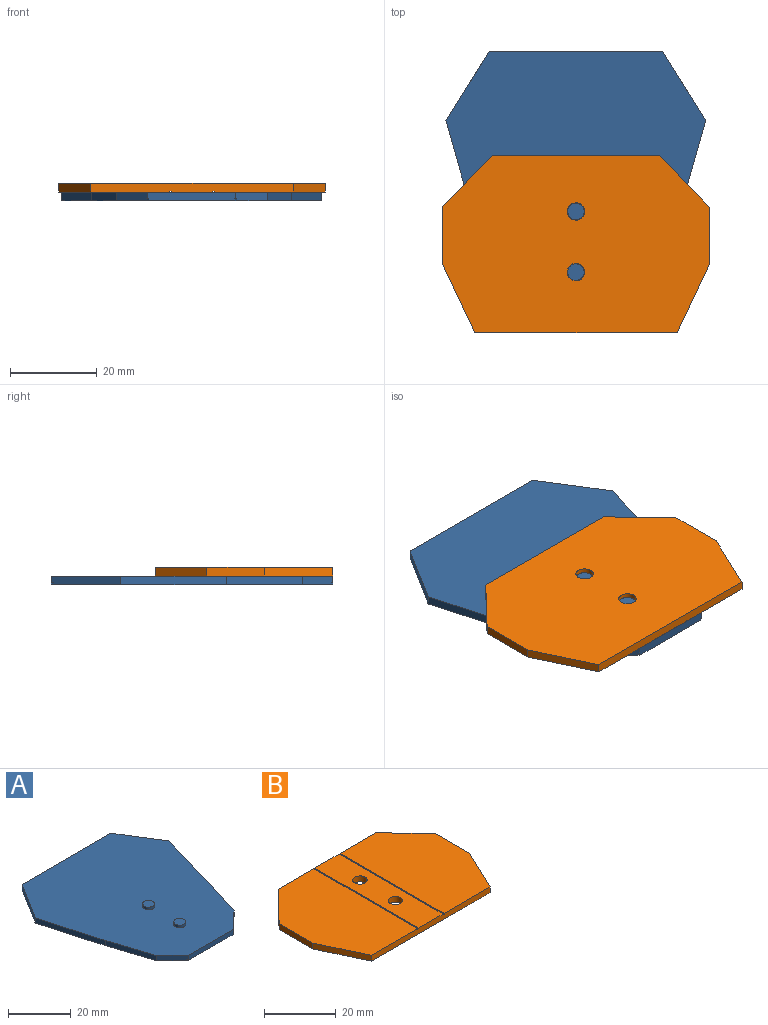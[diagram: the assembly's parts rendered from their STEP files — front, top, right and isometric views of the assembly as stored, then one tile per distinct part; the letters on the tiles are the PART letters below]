
ASSEMBLY  parts=2 mates=1
PART A: 132 faces, bbox 60x65x3 mm
  f0: plane 16x10mm, normal (-0.85,0.53,0), area 37.6mm2, adj f4,f6,f12,f13,f126,f127
  f1: plane 20.31x2mm, normal (0,-1,0), area 40.5mm2, adj f2,f5,f8,f13,f125,f127,f129,f130
  f2: plane 7.24x7mm, normal (0.69,-0.72,0), area 20mm2, adj f1,f3,f9,f13,f128,f130
  f3: plane 64.51x19.61mm, normal (0,0,-1), area 506.2mm2, adj f2,f9,f10,f11,f128
  f4: plane 64.51x19.61mm, normal (0,0,-1), area 507.6mm2, adj f0,f6,f7,f8,f126
  f5: plane 65x39.6mm, normal (0,0,-1), area 1821.7mm2, adj f1,f12,f99,f100,f101,f112,f125,f129
  f6: plane 24.45x6.91mm, normal (-0.96,-0.27,0), area 50.8mm2, adj f0,f4,f7,f13
  f7: plane 17.55x5.69mm, normal (-0.95,-0.31,0), area 36.9mm2, adj f4,f6,f8,f13
  f8: plane 7.24x7mm, normal (-0.69,-0.72,0), area 20mm2, adj f1,f4,f7,f13,f126,f127
  f9: plane 17.51x5.61mm, normal (0.95,-0.31,0), area 36.8mm2, adj f2,f3,f10,f13
  f10: plane 24.49x6.99mm, normal (0.96,-0.27,0), area 50.9mm2, adj f3,f9,f11,f13
  f11: plane 16x10mm, normal (0.85,0.53,0), area 37.6mm2, adj f3,f10,f12,f13,f128,f130
  f12: plane 40x2mm, normal (0,1,0), area 79.8mm2, adj f0,f5,f11,f13,f125,f127,f129,f130
  f13: plane 65x60mm, normal (0,0,1), area 2977.3mm2, adj f0,f1,f2,f6,f7,f8,f9,f10
  f14: cylinder r=1.9mm len=3.8mm, axis (0,0,-1), area 11.9mm2, adj f13,f15
  f15: plane 3.8x3.8mm, normal (0,0,1), area 11.3mm2, adj f14
  f16: cylinder r=1.9mm len=3.8mm, axis (0,0,-1), area 11.9mm2, adj f13,f17
  f17: plane 3.8x3.8mm, normal (0,0,1), area 11.3mm2, adj f16
  f18: plane 0.42x0.4mm, normal (0,1,0), area 0.2mm2, adj f19,f113,f114,f131
  f19: plane 2.21x0.4mm, normal (-1,0,0), area 0.9mm2, adj f18,f20,f114,f131
  f20: plane 1.16x0.4mm, normal (0,1,0), area 0.5mm2, adj f19,f21,f114,f131
  f21: plane 0.4x0.31mm, normal (-1,0,0), area 0.1mm2, adj f20,f22,f114,f131
  f22: plane 1.58x0.4mm, normal (0,-1,0), area 0.6mm2, adj f21,f113,f114,f131
  f23: plane 2.52x0.88mm, normal (-0.94,0.33,0), area 1.1mm2, adj f24,f102,f114,f124
  f24: plane 0.42x0.4mm, normal (0,-1,0), area 0.2mm2, adj f23,f25,f114,f124
  f25: plane 1.89x0.65mm, normal (0.95,-0.33,0), area 0.8mm2, adj f24,f26,f114,f124
  f26: plane 1.89x0.66mm, normal (-0.94,-0.33,0), area 0.8mm2, adj f25,f27,f114,f124
  f27: plane 0.43x0.4mm, normal (0,-1,0), area 0.2mm2, adj f26,f28,f114,f124
  f28: plane 2.52x0.88mm, normal (0.94,0.33,0), area 1.1mm2, adj f27,f102,f114,f124
  f29: plane 0.46x0.4mm, normal (0,1,0), area 0.2mm2, adj f30,f103,f114,f123
  f30: plane 0.4x0.28mm, normal (-0.94,0.34,0), area 0.1mm2, adj f29,f31,f114,f123
  f31: plane 0.65x0.4mm, normal (0,-1,0), area 0.3mm2, adj f30,f103,f114,f123
  f32: extruded ~0.4x0.13mm, area 0.1mm2, adj f33,f104,f114,f122
  f33: extruded ~0.4x0.17mm, area 0.1mm2, adj f32,f34,f114,f122
  f34: extruded ~0.4x0.17mm, area 0.1mm2, adj f33,f35,f114,f122
  f35: extruded ~0.4x0.18mm, area 0.1mm2, adj f34,f36,f114,f122
  f36: extruded ~0.4x0.25mm, area 0.1mm2, adj f35,f37,f114,f122
  f37: extruded ~0.4x0.29mm, area 0.1mm2, adj f36,f38,f114,f122
  f38: extruded ~0.4x0.2mm, area 0.1mm2, adj f37,f39,f114,f122
  f39: extruded ~0.4x0.17mm, area 0.1mm2, adj f38,f40,f114,f122
  f40: extruded ~0.4x0.18mm, area 0.1mm2, adj f39,f41,f114,f122
  f41: extruded ~0.4x0.15mm, area 0.1mm2, adj f40,f42,f114,f122
  f42: extruded ~0.4x0.09mm, area 0mm2, adj f41,f43,f114,f122
  f43: plane 0.4x0.4mm, normal (0,-1,0), area 0.2mm2, adj f42,f44,f114,f122
  f44: plane 0.4x0.3mm, normal (1,0,0), area 0.1mm2, adj f43,f45,f114,f122
  f45: plane 0.4x0.37mm, normal (0,1,0), area 0.1mm2, adj f44,f46,f114,f122
  f46: extruded ~0.4x0.28mm, area 0.1mm2, adj f45,f47,f114,f122
  f47: extruded ~0.4x0.31mm, area 0.1mm2, adj f46,f48,f114,f122
  f48: extruded ~0.4x0.31mm, area 0.1mm2, adj f47,f49,f114,f122
  f49: extruded ~0.4x0.31mm, area 0.1mm2, adj f48,f50,f114,f122
  f50: plane 0.4x0.34mm, normal (0,-1,0), area 0.1mm2, adj f49,f51,f114,f122
  f51: plane 0.4x0.28mm, normal (1,0,0), area 0.1mm2, adj f50,f52,f114,f122
  f52: plane 0.4x0.16mm, normal (0,1,0), area 0.1mm2, adj f51,f53,f114,f122
  f53: extruded ~0.4x0.15mm, area 0.1mm2, adj f52,f54,f114,f122
  f54: extruded ~0.4x0.15mm, area 0.1mm2, adj f53,f55,f114,f122
  f55: extruded ~0.4x0.12mm, area 0.1mm2, adj f54,f56,f114,f122
  f56: extruded ~0.4x0.24mm, area 0.1mm2, adj f55,f57,f114,f122
  f57: extruded ~0.4x0.13mm, area 0.1mm2, adj f56,f58,f114,f122
  f58: extruded ~0.4x0.12mm, area 0.1mm2, adj f57,f59,f114,f122
  f59: extruded ~0.4x0.15mm, area 0.1mm2, adj f58,f60,f114,f122
  f60: extruded ~0.4x0.25mm, area 0.1mm2, adj f59,f61,f114,f122
  f61: plane 0.4x0.13mm, normal (0,-1,0), area 0.1mm2, adj f60,f62,f114,f122
  f62: plane 0.4x0.31mm, normal (1,0,0), area 0.1mm2, adj f61,f63,f114,f122
  f63: plane 0.4x0.18mm, normal (0,1,0), area 0.1mm2, adj f62,f64,f114,f122
  f64: extruded ~0.4x0.31mm, area 0.1mm2, adj f63,f65,f114,f122
  f65: extruded ~0.4x0.27mm, area 0.1mm2, adj f64,f66,f114,f122
  f66: extruded ~0.4x0.21mm, area 0.1mm2, adj f65,f67,f114,f122
  f67: extruded ~0.4x0.31mm, area 0.1mm2, adj f66,f68,f114,f122
  f68: extruded ~0.4x0.19mm, area 0.1mm2, adj f67,f69,f114,f122
  f69: extruded ~0.4x0.15mm, area 0.1mm2, adj f68,f104,f114,f122
  f70: plane 2.52x0.4mm, normal (1,0,0), area 1mm2, adj f71,f105,f114,f121
  f71: plane 0.41x0.4mm, normal (0,1,0), area 0.2mm2, adj f70,f72,f114,f121
  f72: plane 2.52x0.4mm, normal (-1,0,0), area 1mm2, adj f71,f105,f114,f121
  f73: plane 2.52x0.4mm, normal (1,0,0), area 1mm2, adj f74,f106,f114,f120
  f74: plane 0.42x0.4mm, normal (0,1,0), area 0.2mm2, adj f73,f75,f114,f120
  f75: plane 1.56x0.68mm, normal (-0.92,0.4,0), area 0.7mm2, adj f74,f76,f114,f120
  f76: plane 0.63x0.4mm, normal (-1,0,0), area 0.3mm2, adj f75,f77,f114,f120
  f77: plane 0.4x0.11mm, normal (0,-1,0), area 0mm2, adj f76,f78,f114,f120
  f78: plane 1.4x0.57mm, normal (0.93,-0.38,0), area 0.6mm2, adj f77,f79,f114,f120
  f79: plane 1.74x0.4mm, normal (-1,0,0), area 0.7mm2, adj f78,f106,f114,f120
  f80: plane 1.57x0.68mm, normal (0.92,0.4,0), area 0.7mm2, adj f81,f107,f114,f119
  f81: plane 0.42x0.4mm, normal (0,1,0), area 0.2mm2, adj f80,f82,f114,f119
  f82: plane 2.52x0.4mm, normal (-1,0,0), area 1mm2, adj f81,f83,f114,f119
  f83: plane 0.42x0.4mm, normal (0,-1,0), area 0.2mm2, adj f82,f84,f114,f119
  f84: plane 1.74x0.4mm, normal (1,0,0), area 0.7mm2, adj f83,f85,f114,f119
  f85: plane 1.4x0.57mm, normal (-0.93,-0.37,0), area 0.6mm2, adj f84,f86,f114,f119
  f86: plane 0.4x0.11mm, normal (0,-1,0), area 0mm2, adj f85,f107,f114,f119
  f87: plane 2.52x0.4mm, normal (1,0,0), area 1mm2, adj f88,f108,f114,f118
  f88: plane 0.42x0.4mm, normal (0,1,0), area 0.2mm2, adj f87,f89,f114,f118
  f89: plane 2.52x0.4mm, normal (-1,0,0), area 1mm2, adj f88,f108,f114,f118
  f90: plane 0.4x0.28mm, normal (-1,0,0), area 0.1mm2, adj f91,f109,f114,f117
  f91: plane 0.91x0.4mm, normal (0,-1,0), area 0.4mm2, adj f90,f92,f114,f117
  f92: plane 0.4x0.28mm, normal (1,0,0), area 0.1mm2, adj f91,f109,f114,f117
  f93: plane 0.4x0.31mm, normal (1,0,0), area 0.1mm2, adj f94,f110,f114,f116
  f94: plane 1.02x0.4mm, normal (0,1,0), area 0.4mm2, adj f93,f95,f114,f116
  f95: plane 0.4x0.31mm, normal (-1,0,0), area 0.1mm2, adj f94,f110,f114,f116
  f96: plane 1.02x0.4mm, normal (0,1,0), area 0.4mm2, adj f97,f111,f114,f115
  f97: plane 0.4x0.31mm, normal (-1,0,0), area 0.1mm2, adj f96,f98,f114,f115
  f98: plane 1.02x0.4mm, normal (0,-1,0), area 0.4mm2, adj f97,f111,f114,f115
  f99: plane 8x0.4mm, normal (1,0,0), area 3.2mm2, adj f5,f100,f112,f114
  f100: plane 14x0.4mm, normal (0,-1,0), area 5.6mm2, adj f5,f99,f101,f114
  f101: plane 8x0.4mm, normal (-1,0,0), area 3.2mm2, adj f5,f100,f112,f114
  f102: plane 0.41x0.4mm, normal (0,1,0), area 0.2mm2, adj f23,f28,f114,f124
  f103: plane 0.4x0.28mm, normal (0.95,0.33,0), area 0.1mm2, adj f29,f31,f114,f123
  f104: extruded ~0.4x0.12mm, area 0.1mm2, adj f32,f69,f114,f122
  f105: plane 0.41x0.4mm, normal (0,-1,0), area 0.2mm2, adj f70,f72,f114,f121
  f106: plane 0.42x0.4mm, normal (0,-1,0), area 0.2mm2, adj f73,f79,f114,f120
  f107: plane 0.63x0.4mm, normal (1,0,0), area 0.3mm2, adj f80,f86,f114,f119
  f108: plane 0.42x0.4mm, normal (0,-1,0), area 0.2mm2, adj f87,f89,f114,f118
  f109: plane 0.91x0.4mm, normal (0,1,0), area 0.4mm2, adj f90,f92,f114,f117
  f110: plane 1.02x0.4mm, normal (0,-1,0), area 0.4mm2, adj f93,f95,f114,f116
  f111: plane 0.4x0.31mm, normal (1,0,0), area 0.1mm2, adj f96,f98,f114,f115
  f112: plane 14x0.4mm, normal (0,1,0), area 5.6mm2, adj f5,f99,f101,f114
  f113: plane 2.52x0.4mm, normal (1,0,0), area 1mm2, adj f18,f22,f114,f131
  f114: plane 14x8mm, normal (0,0,-1), area 100.8mm2, adj f18,f19,f20,f21,f22,f23,f24,f25
  f115: plane 1.02x0.31mm, normal (0,0,-1), area 0.3mm2, adj f96,f97,f98,f111
  f116: plane 1.02x0.31mm, normal (0,0,-1), area 0.3mm2, adj f93,f94,f95,f110
  f117: plane 0.91x0.28mm, normal (0,0,-1), area 0.3mm2, adj f90,f91,f92,f109
  f118: plane 2.52x0.42mm, normal (0,0,-1), area 1.1mm2, adj f87,f88,f89,f108
  f119: plane 2.52x1.1mm, normal (0,0,-1), area 1.6mm2, adj f80,f81,f82,f83,f84,f85,f86,f107
  f120: plane 2.52x1.1mm, normal (0,0,-1), area 1.6mm2, adj f73,f74,f75,f76,f77,f78,f79,f106
  f121: plane 2.52x0.41mm, normal (0,0,-1), area 1mm2, adj f70,f71,f72,f105
  f122: plane 2.52x1.15mm, normal (0,0,-1), area 1.4mm2, adj f32,f33,f34,f35,f36,f37,f38,f39
  f123: plane 0.65x0.28mm, normal (0,0,-1), area 0.2mm2, adj f29,f30,f31,f103
  f124: plane 2.52x2.17mm, normal (0,0,-1), area 2mm2, adj f23,f24,f25,f26,f27,f28,f102
  f125: plane 65x9.85mm, normal (-0.99,-0.15,0), area 26.3mm2, adj f1,f5,f12,f127
  f126: plane 64.51x9.77mm, normal (0.99,0.15,0), area 26.1mm2, adj f0,f4,f8,f127
  f127: plane 65x10.21mm, normal (0,0,-1), area 26.2mm2, adj f0,f1,f8,f12,f125,f126
  f128: plane 64.51x9.77mm, normal (-0.99,0.15,0), area 26.1mm2, adj f2,f3,f11,f130
  f129: plane 65x9.85mm, normal (0.99,-0.15,0), area 26.3mm2, adj f1,f5,f12,f130
  f130: plane 65x10.21mm, normal (0,0,-1), area 26.2mm2, adj f1,f2,f11,f12,f128,f129
  f131: plane 2.52x1.58mm, normal (0,0,-1), area 1.4mm2, adj f18,f19,f20,f21,f22,f113
PART B: 20 faces, bbox 61.6x41x2 mm
  f0: plane 41x0.4mm, normal (0,0,1), area 16.4mm2, adj f3,f7,f15,f17
  f1: plane 41x0.4mm, normal (0,0,1), area 16.4mm2, adj f3,f7,f13,f18
  f2: plane 15.82x7.44mm, normal (-0.9,-0.43,0), area 35mm2, adj f3,f10,f12,f16
  f3: plane 46.7x2mm, normal (0,-1,0), area 93.2mm2, adj f0,f1,f2,f4,f12,f13,f14,f15
  f4: plane 15.82x7.44mm, normal (0.9,-0.43,0), area 35mm2, adj f3,f5,f12,f14
  f5: plane 13.25x2mm, normal (1,0,0), area 26.5mm2, adj f4,f6,f12,f14
  f6: plane 11.92x11.48mm, normal (0.72,0.69,0), area 33.1mm2, adj f5,f7,f12,f14
  f7: plane 38.55x2mm, normal (0,1,0), area 76.9mm2, adj f0,f1,f6,f8,f12,f13,f14,f15
  f8: plane 11.99x11.55mm, normal (-0.72,0.69,0), area 33.3mm2, adj f7,f10,f12,f16
  f9: cylinder r=2mm len=4mm, axis (0,0,-1), area 25.1mm2, adj f12,f19
  f10: plane 13.19x2mm, normal (-1,0,0), area 26.4mm2, adj f2,f8,f12,f16
  f11: cylinder r=2mm len=4mm, axis (0,0,-1), area 25.1mm2, adj f12,f19
  f12: plane 61.59x41mm, normal (0,0,-1), area 2244.2mm2, adj f2,f3,f4,f5,f6,f7,f8,f9
  f13: plane 41x0.2mm, normal (-1,0,0), area 8.2mm2, adj f1,f3,f7,f14
  f14: plane 41x25.56mm, normal (0,0,1), area 920.5mm2, adj f3,f4,f5,f6,f7,f13
  f15: plane 41x0.2mm, normal (1,0,0), area 8.2mm2, adj f0,f3,f7,f16
  f16: plane 41x25.63mm, normal (0,0,1), area 922.4mm2, adj f2,f3,f7,f8,f10,f15
  f17: plane 41x0.2mm, normal (-1,0,0), area 8.2mm2, adj f0,f3,f7,f19
  f18: plane 41x0.2mm, normal (1,0,0), area 8.2mm2, adj f1,f3,f7,f19
  f19: plane 41x9.6mm, normal (0,0,1), area 368.4mm2, adj f3,f7,f9,f11,f17,f18
PLACE A at identity
PLACE B rot(axis=(0,1,0),180deg) t=(64.97,65,4)mm
MATE fastened B.f11 <-> A.f16  axis (0,0,-1) through (10.15,28,2)mm
